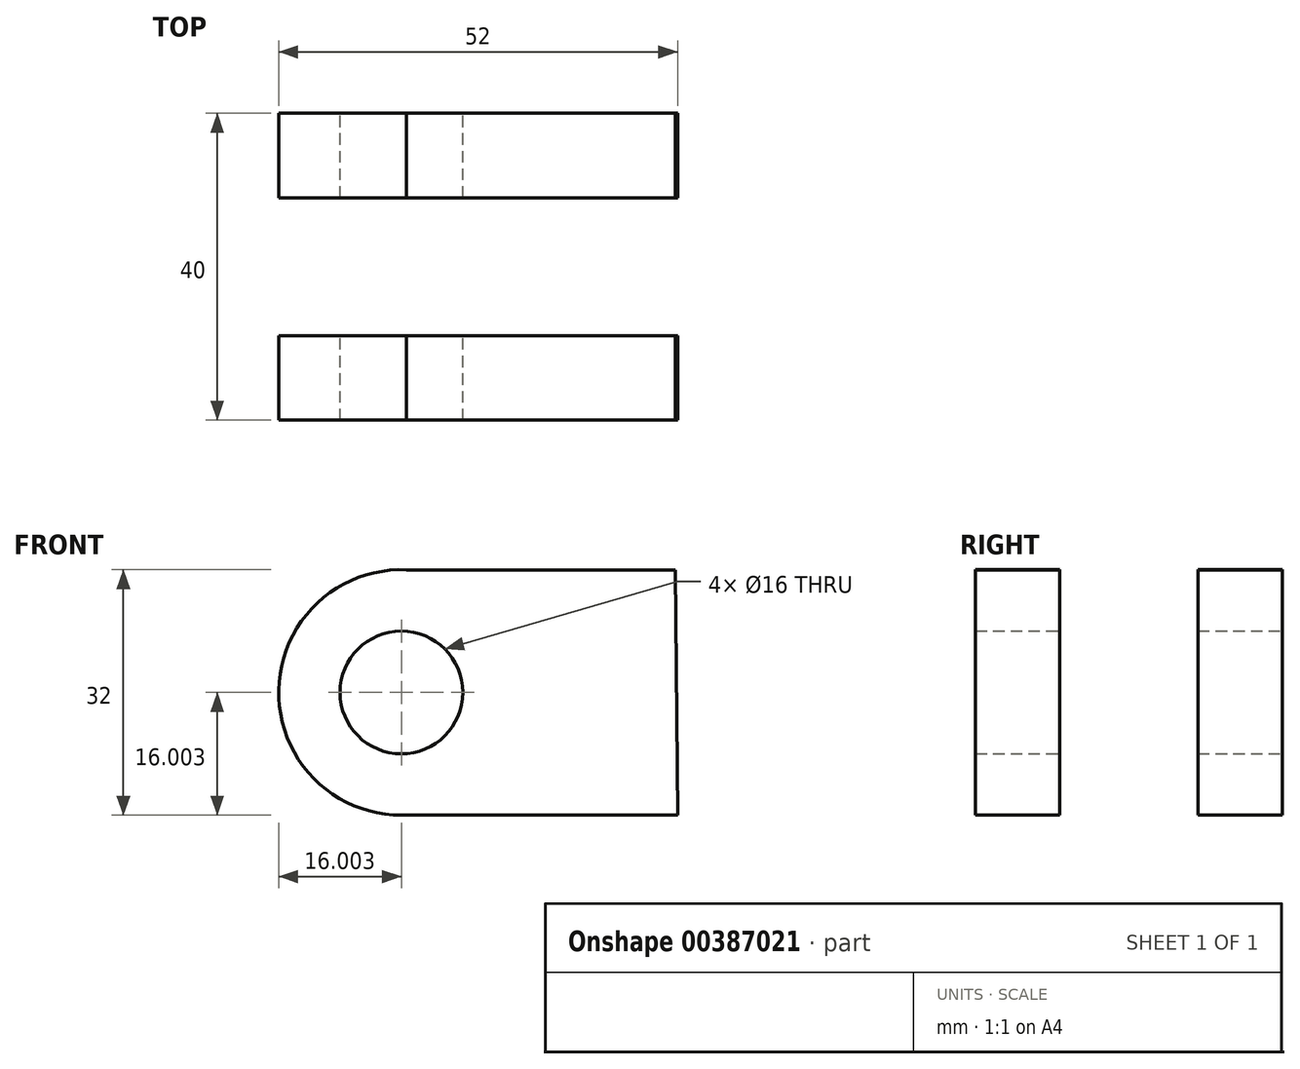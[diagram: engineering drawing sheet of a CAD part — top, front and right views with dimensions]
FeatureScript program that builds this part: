
annotation { "Feature Type Name" : "Feature", "Feature Type Description" : "" }
export const myFeature = defineFeature(function(context is Context, id is Id, definition is map)
    precondition{}
    {
        {
            var Q0;
            Q0=qCreatedBy(makeId("Front.planeOp"),FACE);
            var sketch = newSketch(context, id + "F0", { "sketchPlane" : qUnion([Q0])});
            skLineSegment(sketch, "E0", {"start": v(25.48, 0.76) * mm, "end": v(57.78, 0.76) * mm});
            skLineSegment(sketch, "E1", {"start": v(57.78, -13.65) * mm, "end": v(57.78, 0.76) * mm});
            skLineSegment(sketch, "E2", {"start": v(25.78, -13.65) * mm, "end": v(57.78, -13.65) * mm});
            skLineSegment(sketch, "E3", {"start": v(25.48, 9.52) * mm, "end": v(25.78, -22.47) * mm});
            skLineSegment(sketch, "E4", {"start": v(-9.55, 9.52) * mm, "end": v(25.48, 9.52) * mm});
            skLineSegment(sketch, "E5", {"start": v(-10.22, -22.47) * mm, "end": v(25.78, -22.47) * mm});
            skArc(sketch, "E6", {"start": v(-9.55, 9.52) * mm, "mid": v(-26.21, -6.13) * mm, "end": v(-10.22, -22.47) * mm});
            skCircle(sketch, "E7", {"center": v(-10.22, -6.47) * mm, "radius": 8 * mm});
            skSolve(sketch);
        }
        {
            var Q0;
            Q0 = qSketchRegion(id + "F0", true);
            extrude(context, id + "F1", {"entities" : qUnion([Q0]), "depth" : 11 * mm});
        }
        {
            var Q0;
            Q0=makeQuery(id+"F1.opExtrude","SWEPT_BODY",BODY,{"disambiguationData":[OSD([sQuery(id+"F0.wireOp",EDGE,"E3"),sQuery(id+"F0.wireOp",EDGE,"E4"),sQuery(id+"F0.wireOp",EDGE,"E5"),sQuery(id+"F0.wireOp",EDGE,"E6"),sQuery(id+"F0.wireOp",EDGE,"E7")])]});
            transform(context, id + "F2", {"entities" : qUnion([Q0]), "transformType" : TransformType.TRANSLATION_3D, "dx" : 0 * mm, "dy" : 29 * mm, "dz" : 0 * mm, "makeCopy" : true});
        }
    });
